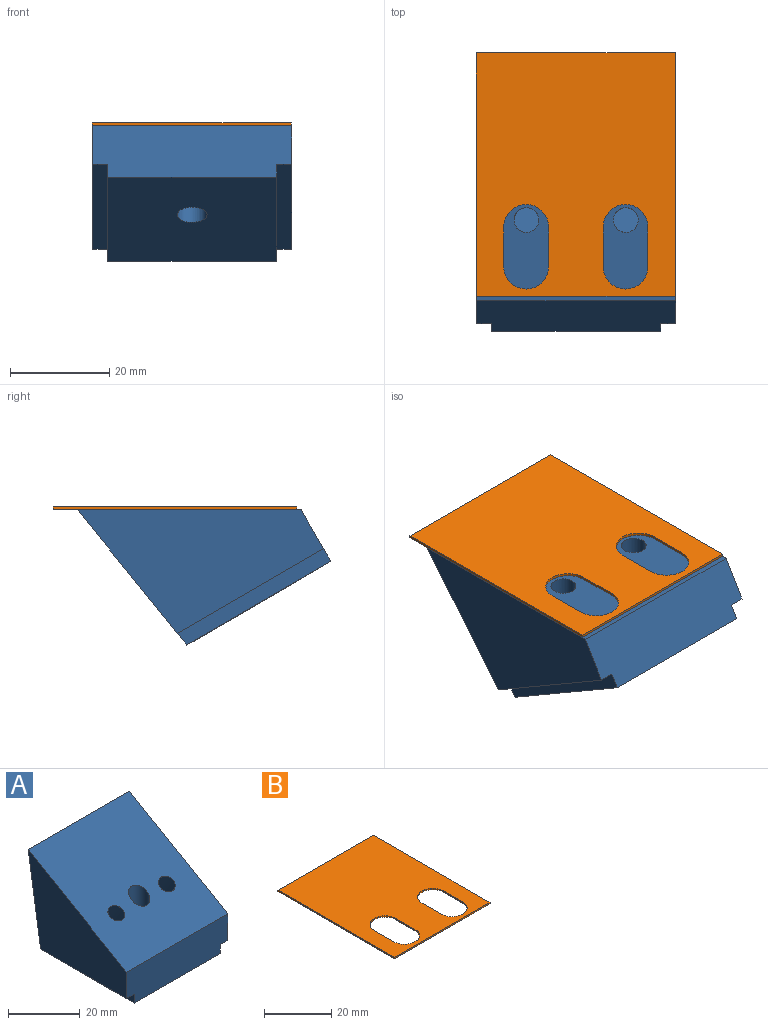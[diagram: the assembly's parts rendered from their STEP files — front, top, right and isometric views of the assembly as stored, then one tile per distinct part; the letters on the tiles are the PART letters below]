
ASSEMBLY  parts=2 mates=1
PART A: 15 faces, bbox 40x38.9x34.6 mm
  f0: plane 34x3mm, normal (0,0,-1), area 102mm2, adj f2,f4,f6,f12
  f1: plane 40x38.9mm, normal (0,-0.5,0.86), area 1728mm2, adj f2,f4,f5,f6,f7,f8,f14
  f2: plane 40x12mm, normal (0,-1,0), area 462mm2, adj f0,f1,f3,f5,f6,f11,f12,f13
  f3: plane 34x3mm, normal (0,0,-1), area 102mm2, adj f2,f4,f5,f11
  f4: plane 40x34.62mm, normal (0,0.99,-0.15), area 1383.2mm2, adj f0,f1,f3,f5,f6,f11,f12,f13
  f5: plane 38.9x31.62mm, normal (1,0,0), area 712.6mm2, adj f1,f2,f3,f4
  f6: plane 38.9x31.62mm, normal (-1,0,0), area 712.6mm2, adj f0,f1,f2,f4
  f7: cylinder r=2.5mm len=17.98mm, axis (0,-0.5,0.86), area 257.9mm2, adj f1,f10
  f8: cylinder r=2.5mm len=17.98mm, axis (0,-0.5,0.86), area 257.9mm2, adj f1,f9
  f9: plane 5.78x5mm, normal (0,0,1), area 22.7mm2, adj f8
  f10: plane 5.78x5mm, normal (0,0,1), area 22.7mm2, adj f7
  f11: plane 34x3mm, normal (1,0,0), area 101.3mm2, adj f2,f3,f4,f13
  f12: plane 34x3mm, normal (-1,0,0), area 101.3mm2, adj f0,f2,f4,f13
  f13: plane 34x33.54mm, normal (0,0,-1), area 1111.9mm2, adj f2,f4,f11,f12,f14
  f14: cylinder r=3mm len=22.49mm, axis (0,0,-1), area 390.6mm2, adj f1,f13
PART B: 14 faces, bbox 40x49x0.5 mm
  f0: cylinder r=4.5mm len=9mm, axis (0,0,-1), area 7.1mm2, adj f1,f11,f12,f13
  f1: plane 8x0.5mm, normal (-1,0,0), area 4mm2, adj f0,f2,f12,f13
  f2: cylinder r=4.5mm len=9mm, axis (0,0,-1), area 7.1mm2, adj f1,f11,f12,f13
  f3: plane 8x0.5mm, normal (-1,0,0), area 4mm2, adj f4,f9,f12,f13
  f4: cylinder r=4.5mm len=9mm, axis (0,0,-1), area 7.1mm2, adj f3,f5,f12,f13
  f5: plane 8x0.5mm, normal (1,0,0), area 4mm2, adj f4,f9,f12,f13
  f6: plane 49x0.5mm, normal (1,0,0), area 24.5mm2, adj f7,f10,f12,f13
  f7: plane 40x0.5mm, normal (0,1,0), area 20mm2, adj f6,f8,f12,f13
  f8: plane 49x0.5mm, normal (-1,0,0), area 24.5mm2, adj f7,f10,f12,f13
  f9: cylinder r=4.5mm len=9mm, axis (0,0,-1), area 7.1mm2, adj f3,f5,f12,f13
  f10: plane 40x0.5mm, normal (0,-1,0), area 20mm2, adj f6,f8,f12,f13
  f11: plane 8x0.5mm, normal (1,0,0), area 4mm2, adj f0,f2,f12,f13
  f12: plane 49x40mm, normal (0,0,1), area 1688.8mm2, adj f0,f1,f2,f3,f4,f5,f6,f7
  f13: plane 49x40mm, normal (0,0,-1), area 1688.8mm2, adj f0,f1,f2,f3,f4,f5,f6,f7
PLACE A rot(axis=(-1,0,0),30.2deg) t=(-37.91,-3.41,-11.14)mm
PLACE B t=(-37.96,-11.26,8.29)mm
MATE parallel A.f1 <-> B.f13  axis (0,0,1) through (-37.91,-13.92,8.2)mm
